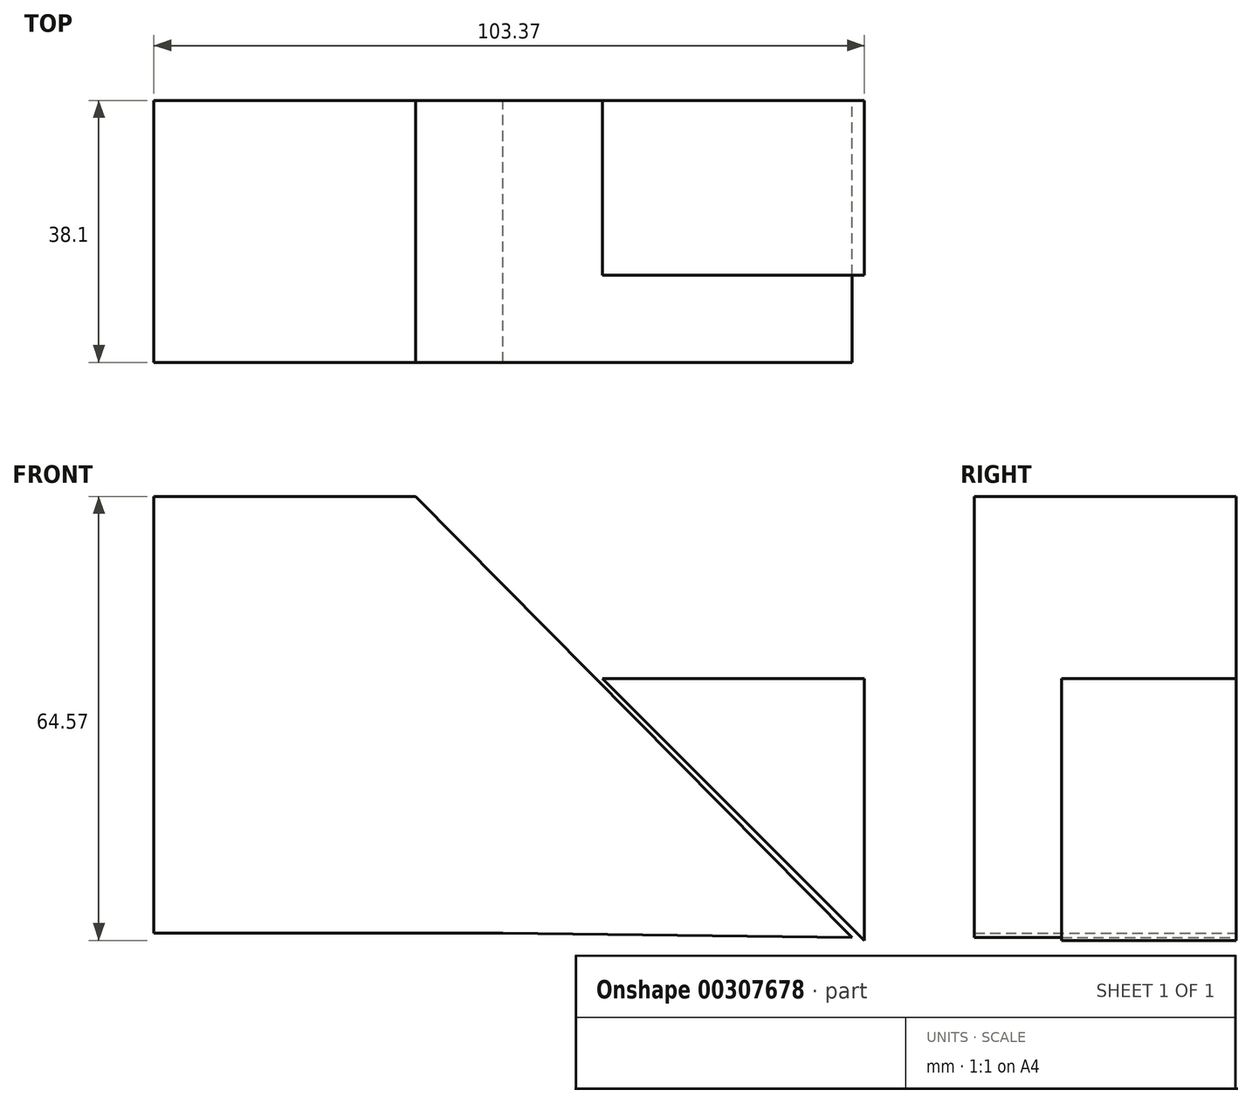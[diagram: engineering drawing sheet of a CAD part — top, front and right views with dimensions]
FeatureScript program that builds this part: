
annotation { "Feature Type Name" : "Feature", "Feature Type Description" : "" }
export const myFeature = defineFeature(function(context is Context, id is Id, definition is map)
    precondition{}
    {
        {
            var Q0;
            Q0=qCreatedBy(makeId("Front.planeOp"),FACE);
            var sketch = newSketch(context, id + "F0", { "sketchPlane" : qUnion([Q0])});
            skLineSegment(sketch, "E0", {"start": v(9.2, -36.83) * mm, "end": v(-41.6, -36.83) * mm});
            skLineSegment(sketch, "E1", {"start": v(-41.6, -36.83) * mm, "end": v(-41.6, 26.67) * mm});
            skLineSegment(sketch, "E2", {"start": v(-41.6, 26.67) * mm, "end": v(-3.5, 26.67) * mm});
            skLineSegment(sketch, "E3", {"start": v(-3.5, 26.67) * mm, "end": v(60, -37.45) * mm});
            skLineSegment(sketch, "E4", {"start": v(60, -37.45) * mm, "end": v(9.2, -36.83) * mm});
            skSolve(sketch);
        }
        {
            var Q0;
            Q0=makeQuery(id+"F0.imprint","IMPRINT",FACE,{"disambiguationData":[TD([[makeQuery(id+"F0.imprint","IMPRINT",EDGE,{"derivedFrom":sQuery(id+"F0.wireOp",EDGE,"E0")}),-1.0]])]});
            extrude(context, id + "F1", {"entities" : qUnion([Q0]), "depth" : 38.1 * mm});
        }
        {
            var Q0;
            Q0=qCreatedBy(makeId("Front.planeOp"),FACE);
            var sketch = newSketch(context, id + "F2", { "sketchPlane" : qUnion([Q0])});
            skLineSegment(sketch, "E5", {"start": v(23.67, 0.2) * mm, "end": v(61.77, -37.9) * mm});
            skLineSegment(sketch, "E6", {"start": v(61.77, -37.9) * mm, "end": v(61.77, 0.2) * mm});
            skLineSegment(sketch, "E7", {"start": v(61.77, 0.2) * mm, "end": v(23.67, 0.2) * mm});
            skSolve(sketch);
        }
        {
            var Q0;
            Q0=makeQuery(id+"F2.imprint","IMPRINT",FACE,{"disambiguationData":[TD([[makeQuery(id+"F2.imprint","IMPRINT",EDGE,{"derivedFrom":sQuery(id+"F2.wireOp",EDGE,"E5")}),1.0]])]});
            extrude(context, id + "F3", {"entities" : qUnion([Q0]), "operationType" : NewBodyOperationType.ADD, "depth" : 25.4 * mm});
        }
    });
